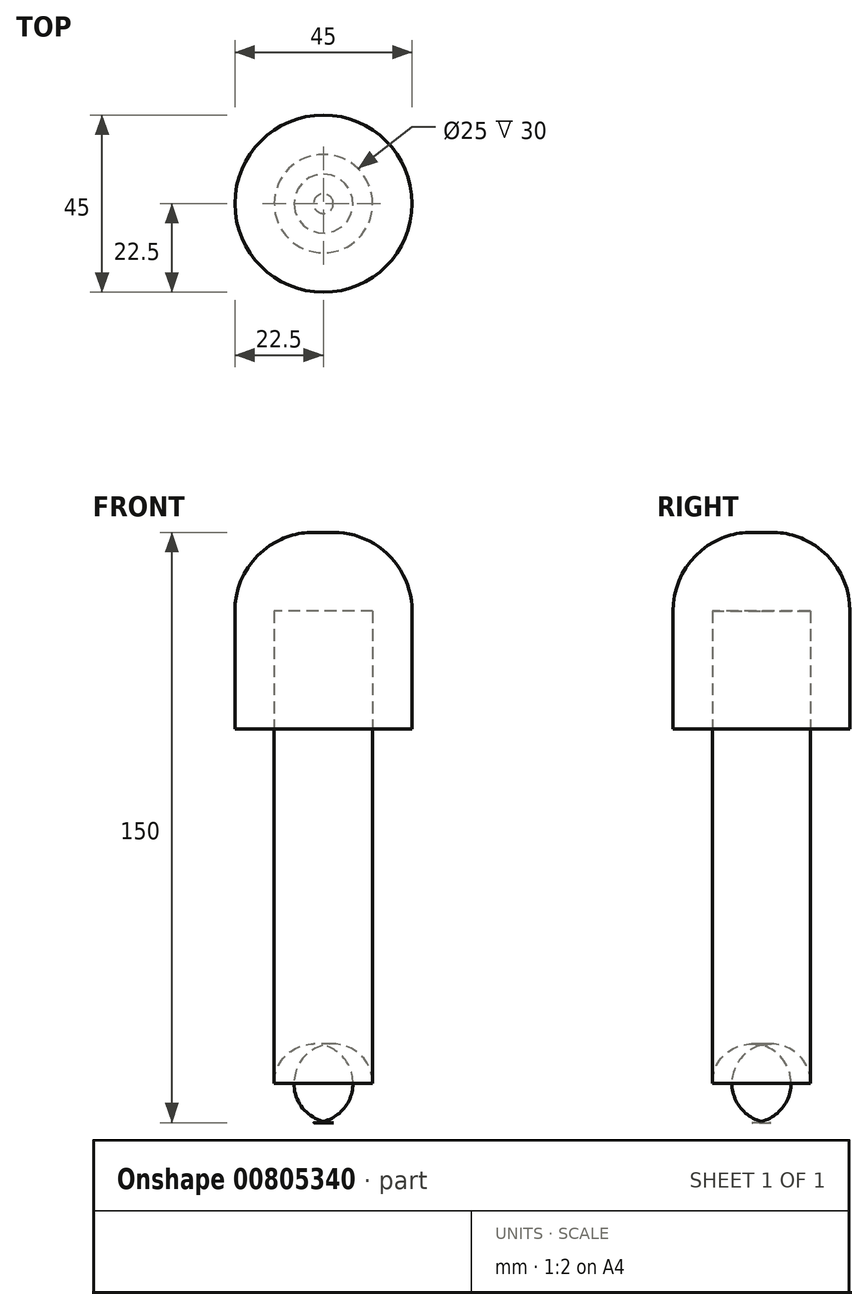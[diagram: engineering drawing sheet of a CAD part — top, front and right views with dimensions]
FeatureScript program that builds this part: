
annotation { "Feature Type Name" : "Feature", "Feature Type Description" : "" }
export const myFeature = defineFeature(function(context is Context, id is Id, definition is map)
    precondition{}
    {
        {
            var Q0;
            Q0=qCreatedBy(makeId("Top.planeOp"),FACE);
            var sketch = newSketch(context, id + "F0", { "sketchPlane" : qUnion([Q0])});
            skCircle(sketch, "E0", {"center": v(0, 0) * mm, "radius": 22.5 * mm});
            skCircle(sketch, "E1", {"center": v(0, 0) * mm, "radius": 12.5 * mm});
            skSolve(sketch);
        }
        {
            var Q0;
            Q0=makeQuery(id+"F0.imprint","IMPRINT",FACE,{"disambiguationData":[TD([[makeQuery(id+"F0.imprint","IMPRINT",EDGE,{"derivedFrom":sQuery(id+"F0.wireOp",EDGE,"E0")}),1.0]])]});
            extrude(context, id + "F1", {"entities" : qUnion([Q0]), "depth" : 30 * mm, "offsetDistance" : 25.4 * mm});
        }
        {
            var Q0;
            Q0=makeQuery(id+"F0.imprint","IMPRINT",FACE,{"disambiguationData":[TD([[makeQuery(id+"F0.imprint","IMPRINT",EDGE,{"derivedFrom":sQuery(id+"F0.wireOp",EDGE,"E1")}),1.0]])]});
            extrude(context, id + "F2", {"entities" : qUnion([Q0]), "operationType" : NewBodyOperationType.ADD, "oppositeDirection" : true, "depth" : 100 * mm, "offsetDistance" : 25.4 * mm});
        }
        {
            var Q0;
            Q0=makeQuery(id+"F2.opExtrude","CAP_FACE",FACE,{"disambiguationData":[OSD([sQuery(id+"F0.wireOp",EDGE,"E1")])],"isStart":false});
            fillet(context, id + "F3", {"entities" : qUnion([Q0]), "radius" : 10 * mm, "tangentPropagation" : true, "allowEdgeOverflow" : false});
        }
        {
            var Q0;
            Q0=makeQuery(id+"F1.opExtrude","CAP_FACE",FACE,{"disambiguationData":[OSD([sQuery(id+"F0.wireOp",EDGE,"E0"),sQuery(id+"F0.wireOp",EDGE,"E1")])],"isStart":false});
            var sketch = newSketch(context, id + "F4", { "sketchPlane" : qUnion([Q0])});
            skCircle(sketch, "E2", {"center": v(0, 0) * mm, "radius": 22.5 * mm});
            skSolve(sketch);
        }
        {
            var Q0;
            Q0 = qSketchRegion(id + "F4", true);
            extrude(context, id + "F5", {"entities" : qUnion([Q0]), "operationType" : NewBodyOperationType.ADD, "depth" : 20 * mm, "offsetDistance" : 25.4 * mm});
        }
        {
            var Q0;
            Q0=makeQuery(id+"F5.opExtrude","CAP_FACE",FACE,{"disambiguationData":[OSD([sQuery(id+"F4.wireOp",EDGE,"E2")])],"isStart":false});
            fillet(context, id + "F6", {"entities" : qUnion([Q0]), "radius" : 20 * mm, "tangentPropagation" : true, "allowEdgeOverflow" : false});
        }
    });
